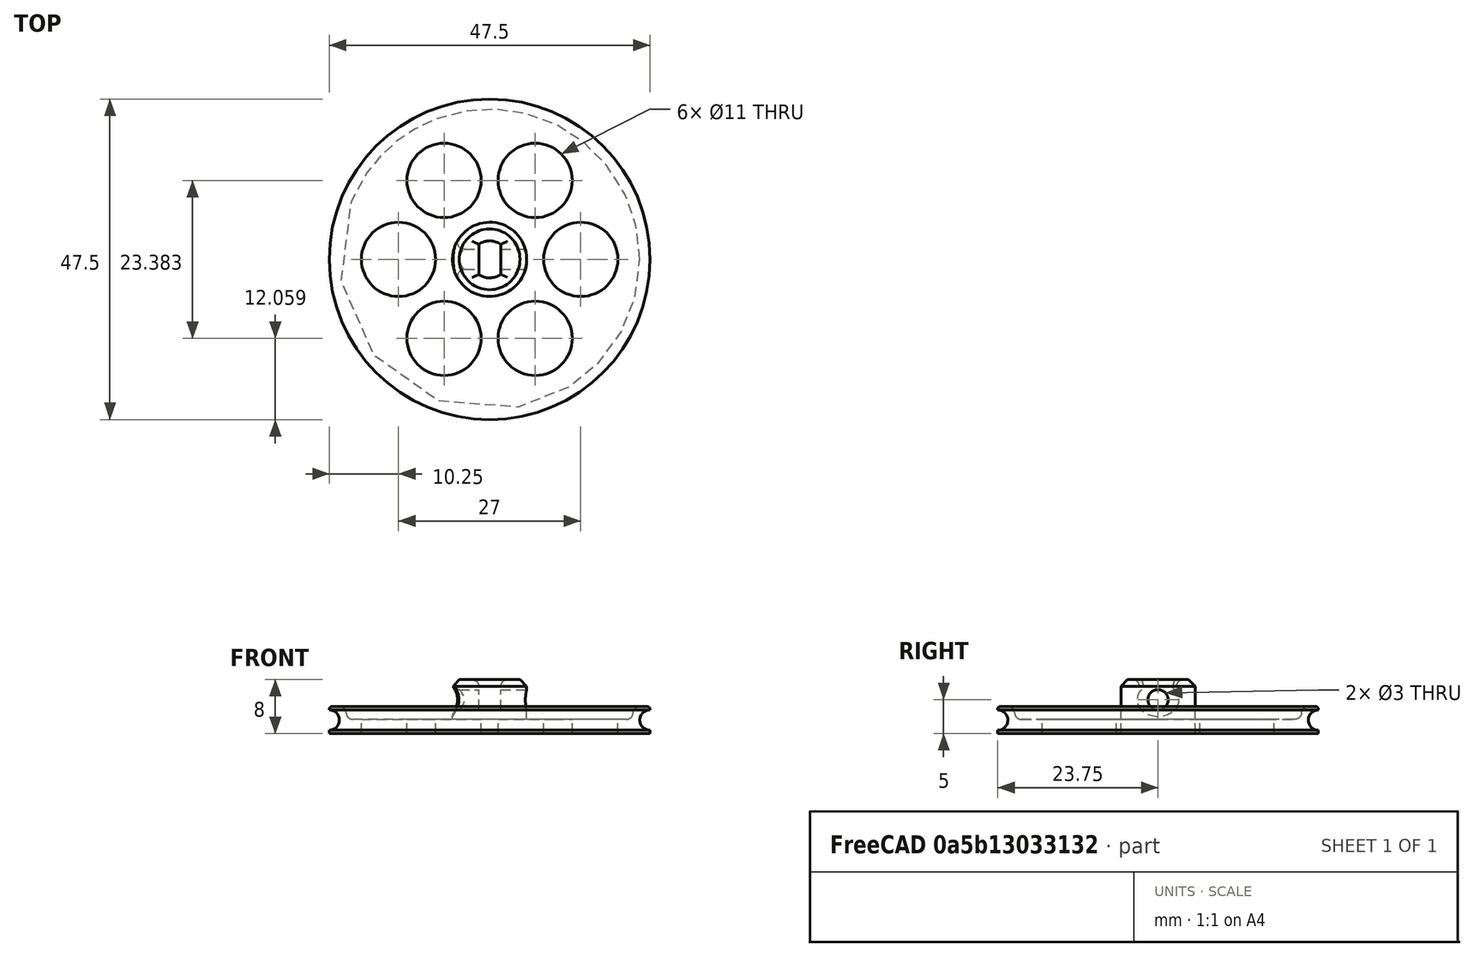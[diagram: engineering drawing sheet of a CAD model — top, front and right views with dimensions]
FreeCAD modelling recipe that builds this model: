
FCSTD DOCUMENT  (FreeCAD 0.16R6712 (Git))
Label: wheel_v01
License: All rights reserved
LicenseURL: http://en.wikipedia.org/wiki/All_rights_reserved
objects: Part::Cylinder×6, Part::Cut×5, PartDesign::Fillet×5, Sketcher::SketchObject×1, Part::Torus×1, Part::Box×1, Part::MultiCommon×1, Part::FeaturePython×1, Drawing::FeaturePage×1, Part::MultiFuse×1, Spreadsheet::Sheet×1, PartDesign::Chamfer×1
note: 23 computed .brp shape members not serialized (recipe doc carries the construction recipe); baked Part::Feature solids carry a one-line shape summary decoded from their .brp

FEATURE [Sketcher::SketchObject] Sketch
FEATURE [Part::Torus] Torus
  Angle1 = -180
  Angle2 = 180
  Angle3 = 360
  Placement = pos=(0,0,2) rot=(0,0,1;0rad)
  Radius1 = 23.75
  Radius2 = 1.5
  expr: Radius1 = data.wheel_radius
FEATURE [Part::Cylinder] Cylinder
  Angle = 360
  Height = 4
  Radius = 23.75
  expr: Height = data.rim_thickness
  expr: Radius = data.wheel_radius
FEATURE [Part::Cut] Cut  label="rim"
  Base = -> Cylinder
  Tool = -> Torus
FEATURE [Part::Cylinder] Cylinder001  label="hub"
  Angle = 360
  Height = 8
  Radius = 5.5
FEATURE [Part::Cylinder] Cylinder002  label="Cylinder001"
  Angle = 360
  Height = 12
  Radius = 2.75
FEATURE [Part::Box] Box  label="Cube"
  Height = 12
  Length = 3.25
  Placement = pos=(-1.6125,-6,0) rot=(0,0,1;0rad)
  Width = 12
FEATURE [Part::MultiCommon] Common  label="shaft"
  Shapes = -> [Box,Cylinder002]
FEATURE [Part::Cylinder] Cylinder003  label="setscrew"
  Angle = 360
  Height = 20
  Placement = pos=(-10,0,5) rot=(0,1,0;1.5708rad)
  Radius = 1.5
FEATURE [Part::Cylinder] Cylinder004  label="spoke"
  Angle = 360
  Height = 20
  Placement = pos=(13.5,0,0) rot=(0,0,1;0rad)
  Radius = 5.5
FEATURE [Part::FeaturePython] Array  # Draft array (typed FeaturePython)
  Angle = 360
  ArrayType = 1
  Axis = (0,0,1)
  Base = -> Cylinder004
  Center = (0,0,0)
  Fuse = false
  IntervalAxis = (0,0,0)
  IntervalX = (1,0,0)
  IntervalY = (0,1,0)
  IntervalZ = (0,0,0)
  NumberPolar = 6
  NumberX = 1
  NumberY = 2
  NumberZ = 1
FEATURE [Drawing::FeaturePage] Page
  EditableTexts = AUTHOR NAME | CREATION DATE | SUPERVISOR NAME | CHECK DATE | SCALE | WEIGHT | NUMBER | SHEET | TITLE | SUBTITLE
FEATURE [Part::Cylinder] Cylinder005  label="Cylinder002"
  Angle = 360
  Height = 10
  Placement = pos=(0,0,2.1) rot=(0,0,1;0rad)
  Radius = 21.25
  expr: Radius = 21.25mm
FEATURE [Part::Cut] Cut002
  Base = -> Cut
  Tool = -> Cylinder005
FEATURE [Part::MultiFuse] Fusion
  Shapes = -> [Cylinder001,Cut002]
FEATURE [Part::Cut] Cut003
  Base = -> Fusion
  Tool = -> Common
FEATURE [Part::Cut] Cut004
  Base = -> Cut003
  Tool = -> Cylinder003
FEATURE [Part::Cut] Cut005
  Base = -> Cut004
  Tool = -> Array
FEATURE [Spreadsheet::Sheet] Spreadsheet  label="data"
  cells = A3=wheel_diameter; B3(wheel_diameter)==47.5mm
FEATURE [PartDesign::Fillet] Fillet
  Base = -> Cut005 [Edge4,Edge3,Edge2,Edge5]
  Radius = 1
FEATURE [PartDesign::Fillet] Fillet002
  Base = -> Fillet [Edge35]
  Radius = 1
FEATURE [PartDesign::Fillet] Fillet003
  Base = -> Fillet002 [Edge35]
  Radius = 1
FEATURE [PartDesign::Fillet] Fillet004
  Base = -> Fillet003 [Edge13]
  Radius = 0.4
FEATURE [PartDesign::Fillet] Fillet005
  Base = -> Fillet004 [Edge31]
  Radius = 1
FEATURE [PartDesign::Chamfer] Chamfer
  Base = -> Fillet005 [Edge7]
  Size = 1
